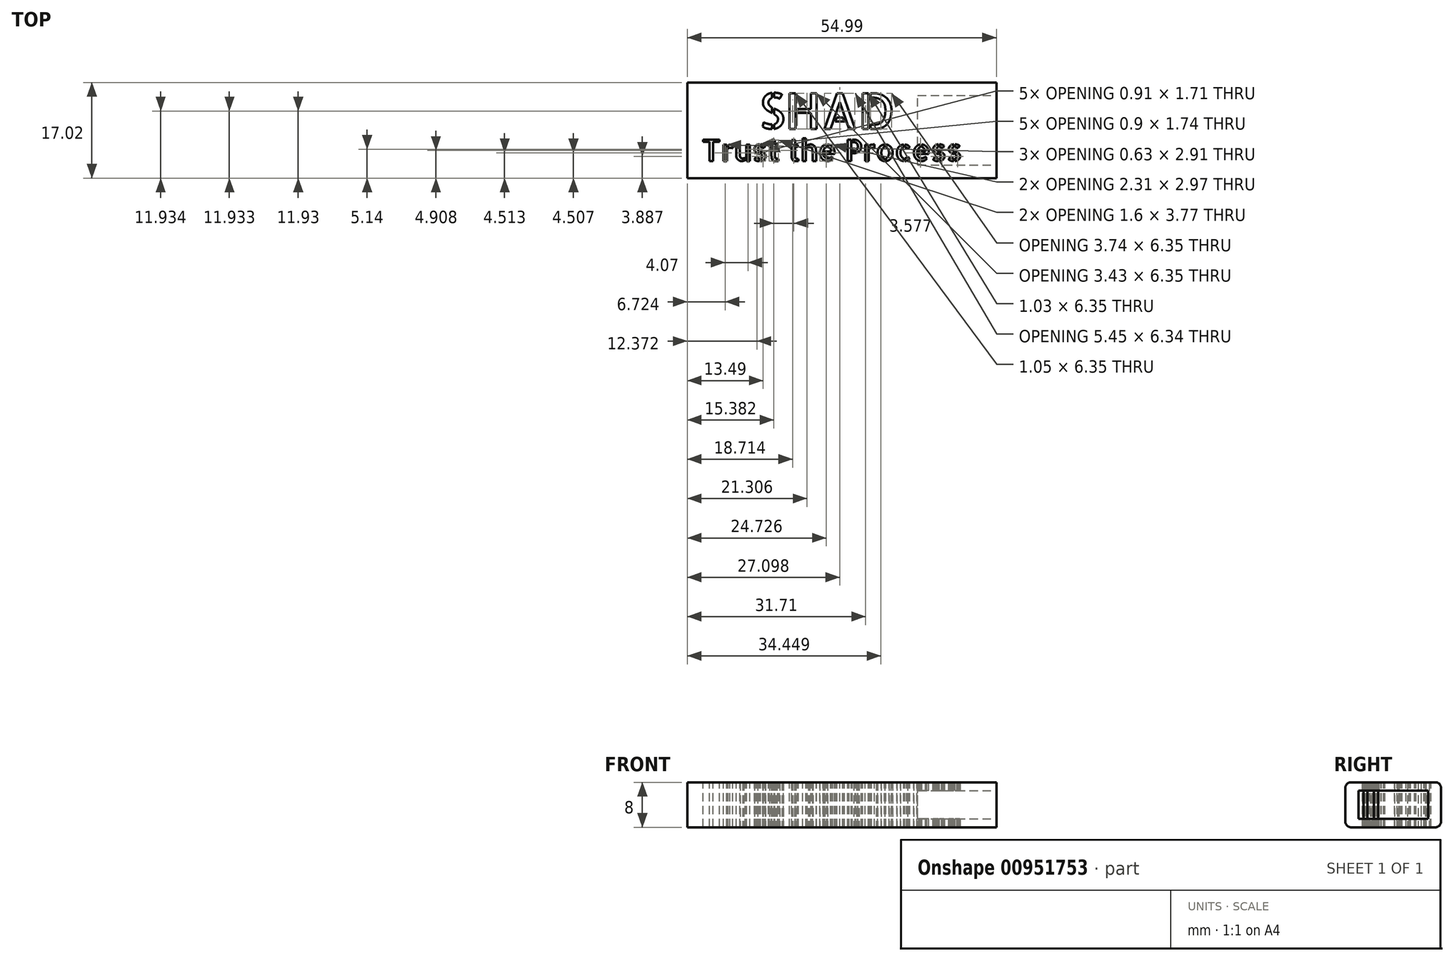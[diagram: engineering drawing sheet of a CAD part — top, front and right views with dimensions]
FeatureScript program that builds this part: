
annotation { "Feature Type Name" : "Feature", "Feature Type Description" : "" }
export const myFeature = defineFeature(function(context is Context, id is Id, definition is map)
    precondition{}
    {
        {
            var Q0;
            Q0=qCreatedBy(makeId("Front.planeOp"),FACE);
            var sketch = newSketch(context, id + "F0", { "sketchPlane" : qUnion([Q0])});
            skLineSegment(sketch, "E0.bottom", {"start": v(-7.52, -4) * mm, "end": v(7.52, -4) * mm});
            skLineSegment(sketch, "E0.top", {"start": v(-7.52, 4) * mm, "end": v(7.52, 4) * mm});
            skLineSegment(sketch, "E0.left", {"start": v(-8.5, -3) * mm, "end": v(-8.5, 3) * mm});
            skLineSegment(sketch, "E0.right", {"start": v(8.5, -3) * mm, "end": v(8.5, 3) * mm});
            skPoint(sketch, "E1.visualSharp", {"position": v(-8.5, 4) * mm});
            skArc(sketch, "E1.filletArc", {"start": v(-7.52, 4) * mm, "mid": v(-8.22, 3.71) * mm, "end": v(-8.5, 3) * mm});
            skPoint(sketch, "E2.visualSharp", {"position": v(8.5, 4) * mm});
            skArc(sketch, "E2.filletArc", {"start": v(8.5, 3) * mm, "mid": v(8.22, 3.71) * mm, "end": v(7.52, 4) * mm});
            skPoint(sketch, "E3.visualSharp", {"position": v(8.5, -4) * mm});
            skArc(sketch, "E3.filletArc", {"start": v(7.52, -4) * mm, "mid": v(8.22, -3.71) * mm, "end": v(8.5, -3) * mm});
            skPoint(sketch, "E4.visualSharp", {"position": v(-8.5, -4) * mm});
            skArc(sketch, "E4.filletArc", {"start": v(-8.5, -3) * mm, "mid": v(-8.22, -3.71) * mm, "end": v(-7.52, -4) * mm});
            skSolve(sketch);
        }
        {
            var Q0;
            Q0 = qSketchRegion(id + "F0", true);
            extrude(context, id + "F1", {"entities" : qUnion([Q0]), "depth" : 55 * mm, "offsetDistance" : 25.4 * mm});
        }
        {
            var Q0;
            Q0=makeQuery(id+"F1.opExtrude","CAP_FACE",FACE,{"disambiguationData":[OSD([sQuery(id+"F0.wireOp",EDGE,"E0.bottom"),sQuery(id+"F0.wireOp",EDGE,"E0.top"),sQuery(id+"F0.wireOp",EDGE,"E0.left"),sQuery(id+"F0.wireOp",EDGE,"E0.right"),sQuery(id+"F0.wireOp",EDGE,"E1.filletArc"),sQuery(id+"F0.wireOp",EDGE,"E2.filletArc"),sQuery(id+"F0.wireOp",EDGE,"E3.filletArc"),sQuery(id+"F0.wireOp",EDGE,"E4.filletArc")])],"isStart":false});
            var sketch = newSketch(context, id + "F2", { "sketchPlane" : qUnion([Q0])});
            skLineSegment(sketch, "E5.bottom", {"start": v(-6.2, 2.5) * mm, "end": v(6.2, 2.5) * mm});
            skLineSegment(sketch, "E5.top", {"start": v(-6.2, -2.5) * mm, "end": v(6.2, -2.5) * mm});
            skLineSegment(sketch, "E5.left", {"start": v(-6.2, 2.5) * mm, "end": v(-6.2, -2.5) * mm});
            skLineSegment(sketch, "E5.right", {"start": v(6.2, 2.5) * mm, "end": v(6.2, -2.5) * mm});
            skSolve(sketch);
        }
        {
            var Q0;
            Q0 = qSketchRegion(id + "F2", true);
            extrude(context, id + "F3", {"entities" : qUnion([Q0]), "operationType" : NewBodyOperationType.REMOVE, "oppositeDirection" : true, "depth" : 14 * mm, "offsetDistance" : 25.4 * mm});
        }
        {
            var Q0;
            Q0=makeQuery(id+"F1.opExtrude","SWEPT_BODY",BODY,{"disambiguationData":[OSD([sQuery(id+"F0.wireOp",EDGE,"E0.bottom"),sQuery(id+"F0.wireOp",EDGE,"E0.top"),sQuery(id+"F0.wireOp",EDGE,"E0.left"),sQuery(id+"F0.wireOp",EDGE,"E0.right"),sQuery(id+"F0.wireOp",EDGE,"E1.filletArc"),sQuery(id+"F0.wireOp",EDGE,"E2.filletArc"),sQuery(id+"F0.wireOp",EDGE,"E3.filletArc"),sQuery(id+"F0.wireOp",EDGE,"E4.filletArc")])]});
            var Q1;
            Q1=makeQuery(id+"F1.opExtrude","CAP_EDGE",EDGE,{"disambiguationData":[OSD([sQuery(id+"F0.wireOp",EDGE,"E0.left")])],"isStart":true});
            transform(context, id + "F4", {"entities" : qUnion([Q0]), "transformType" : TransformType.ROTATION, "transformAxis" : qUnion([Q1]), "angle" : 90 * degree, "makeCopy" : false});
        }
        {
            var Q0;
            Q0=makeQuery(id+"F1.opExtrude","SWEPT_FACE",FACE,{"disambiguationData":[OSD([sQuery(id+"F0.wireOp",EDGE,"E0.top")])]});
            var sketch = newSketch(context, id + "F5", { "sketchPlane" : qUnion([Q0])});
            skText(sketch, "E6", { "text": "SHAD", "fontName": "AllertaStencil-Regular.ttf"});
            skText(sketch, "E7", { "text": "Trust the Process\n", "fontName": "AllertaStencil-Regular.ttf"});
            const initialGuessF5  = {"E6": [0.0042, 0.00876, 1, 0, 0.00635], "E7": [-0.00597, 0.00305, 1, 0, 0.00381]};
            skSetInitialGuess(sketch, initialGuessF5);
            skSolve(sketch);
        }
        {
            var Q0;
            Q0 = qSketchRegion(id + "F5", true);
            extrude(context, id + "F6", {"entities" : qUnion([Q0]), "operationType" : NewBodyOperationType.REMOVE, "oppositeDirection" : true, "depth" : 11.43 * mm, "offsetDistance" : 25.4 * mm});
        }
    });
